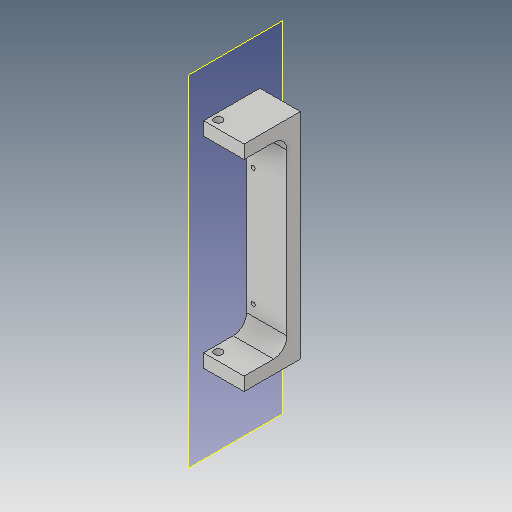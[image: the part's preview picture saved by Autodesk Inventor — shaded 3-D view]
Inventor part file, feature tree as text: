
AUTODESK INVENTOR PART (.ipt)
format: ipt  version: 2019.4 (Build 234330000, 330)  size: 125,440 bytes
history: native  units: mm
features: other x11, reference x6, sketch x3, plane x2, extrude x2, hole x1, projected_geometry x1
ambient origin geometry x8: Origin, YZ Plane, XZ Plane, XY Plane, X Axis, Y Axis, Z Axis, Center Point
bodies: Solid1 (feature_tree)
feature tree (26):
  plane  "Work Plane1"
  sketch  "Sketch1"  dims[d0=10.0mm d1=10.0mm]
  plane  "Work Plane2"
  extrude  "Extrusion1"  Depth=10.0mm
  extrude  "Extrusion2"  Depth=10.0mm
  hole  "Hole1"  [1 undecoded]
  reference  "Reference1"
  reference  "Reference2"
  reference  "Reference3"
  sketch  "Sketch2"  dims[d2=42.0mm d3=10.0mm]
  projected_geometry  "Projected Loop1"
  sketch  "Sketch3"  dims[d4=140.0mm d5=10.0mm d6=10.0mm d7=0.0mm d8=6.0mm d9=10.0mm d10=0.0mm d11=2.9mm d12=6.0mm d13=4.0mm d14=2.0mm d15=90.0deg d16=8.0mm d17=20.594885mm d18=0.0mm d19=6.0mm]
  reference  "Reference4"
  reference  "Reference5"
  reference  "Reference6"
  other  "Assembly_Opentrons_Imagingunit_v2.iam"
  other  "Assembly_opentrons_microscope_slide_y_base:1"
  other  "02_Opentrons_Microscope_Base_v0:1"
  other  "Assembly_Opentrons_Imagingunit_v1.iam"
  other  "Assembly_opentrons_microscope_slide_y:1"
  other  "Assembly_spindeldrive_350mm:1"
  other  "00_spindel_350mm:1"
  other  "Assembly_Opentrons_Autofocus_v1:1"
  other  "01_Slide_camera_x_rail:1"
  other  "04_OPENTRONS_Microscope_wellplate_base:1"
  other  "09_Opentrons_Microscope_Baseplate:1"
note: 1 required parameter value undecoded (feature->parameter linkage not recoverable at this tier; creation-order binding heuristic only, values carry confidence <= 0.55)
